# Revit family: LR1677
name_source: partatom
category: Plumbing Fixtures
units: mm (PartAtom-declared; Revit-internal decimal feet)

## family parameters
Cut with Voids When Loaded = No
Host = Face
Maintain Annotation Orientation = No
OmniClass Number = 23.45.05.14.14
OmniClass Title = Sinks/Lavatories
Part Type = Normal
Room Calculation Point = No
Round Connector Dimension = Use Diameter
Shared = Yes

## types (2) — shared parameters
-1 Off-Floor, Wall Outlet = Yes
-BRS Brass Body Valve = No
-CI Cycle Interrupt for Time-Trol Valves = No
-EG Enviro-Glaze = No
-FMT Fixture Mounted Trim = No
-LW1 Thru-Wall Waste Extension with P-Trap = No
-LWE Lavy Waste Extension (11” Standard) = No
-MA2 Manifolded, 2-Stack = No
-MA3 Manifolded, 3-Stack = No
-MA4 Manifolded, 4-Stack = No
-MT Metal Template = No
-SW Wall Sleeve = No
-TF Transformer, 120VAC to 24VAC (-MVC option only) = No
-TG 12 Gage Cabinet = No
-THLR (Double) Towel Hook = Yes
-THLR (Single) Towel Hook = No
-VAC AcornVac System = No
ADA Compliant = Yes
Assembly Code = D2010400
Basin Shape = D-Shaped Bowl
Bowl Depth = 3 1/2"
CW Connection = Yes
CWFU = 1.5
Cold Water Connection Diameter = 1/2"
Compliance Certifications = ANSI, UFAS, CBC, and ADA 2010
Default Elevation = 0"
Description = Secur-Care - Ligature Resistant LR1677 Series
Finish = Stainless Steel-Bobrick-Satin
HW Connection = Yes
HWFU = 1.5
Height = 14 3/4"
Hot Water Connection Diameter = 1/2"
Installation Instruction Link = https://www.acorneng.com
Installation Type = Wall Mounted
Length = 18"
Manufacturer = Acorn
Material = Stainless Steel-Bobrick-Satin
Price = Prices may vary. Please consult Manufacturer Representative for most up-to-date price list.
Product Documentation Link = https://www.acorneng.com
Product Page URL = https://www.acorneng.com
Rim Width = 13"
URL = https://www.acorneng.com
Valve = Valve Type : -04-M Valve (Pneumatic) Air-Trol - Hot & Cold, Metering
Valve Inlet Distance from Inner Wall (min. 8" to max 28") = 18"
Valve Inlet Height from Floor (min. 26" to max. 46") = 26"
Vent Connection = No
WFU = 2
Waste Connection = Yes
Waste Connection Diameter = 1 1/2"
Waste Connection Height = 27 1/2"
Width = 29 1/2"
valve (R) distance = 47 1/2"
valve L constrait = 11 1/2"
valve R constraint = 47 1/2"
valve_distance_constraint = 18"
valve_height = 26"

## per-type parameters (varying)
| type | -L Left Hand Corner | -R Right Hand Corner | Connections to Center Distance | valve_distance |
| LR1677-1-L-04 | Yes | No | 0" | 11 1/2" |
| LR1677-1-R-04 | No | Yes | 36" | 47 1/2" |

note: column(s) folded — value = type name in every type: Model

## geometry (parser evidence)
native form markers: Sweep x3
no freeform markers — native parametric forms only
